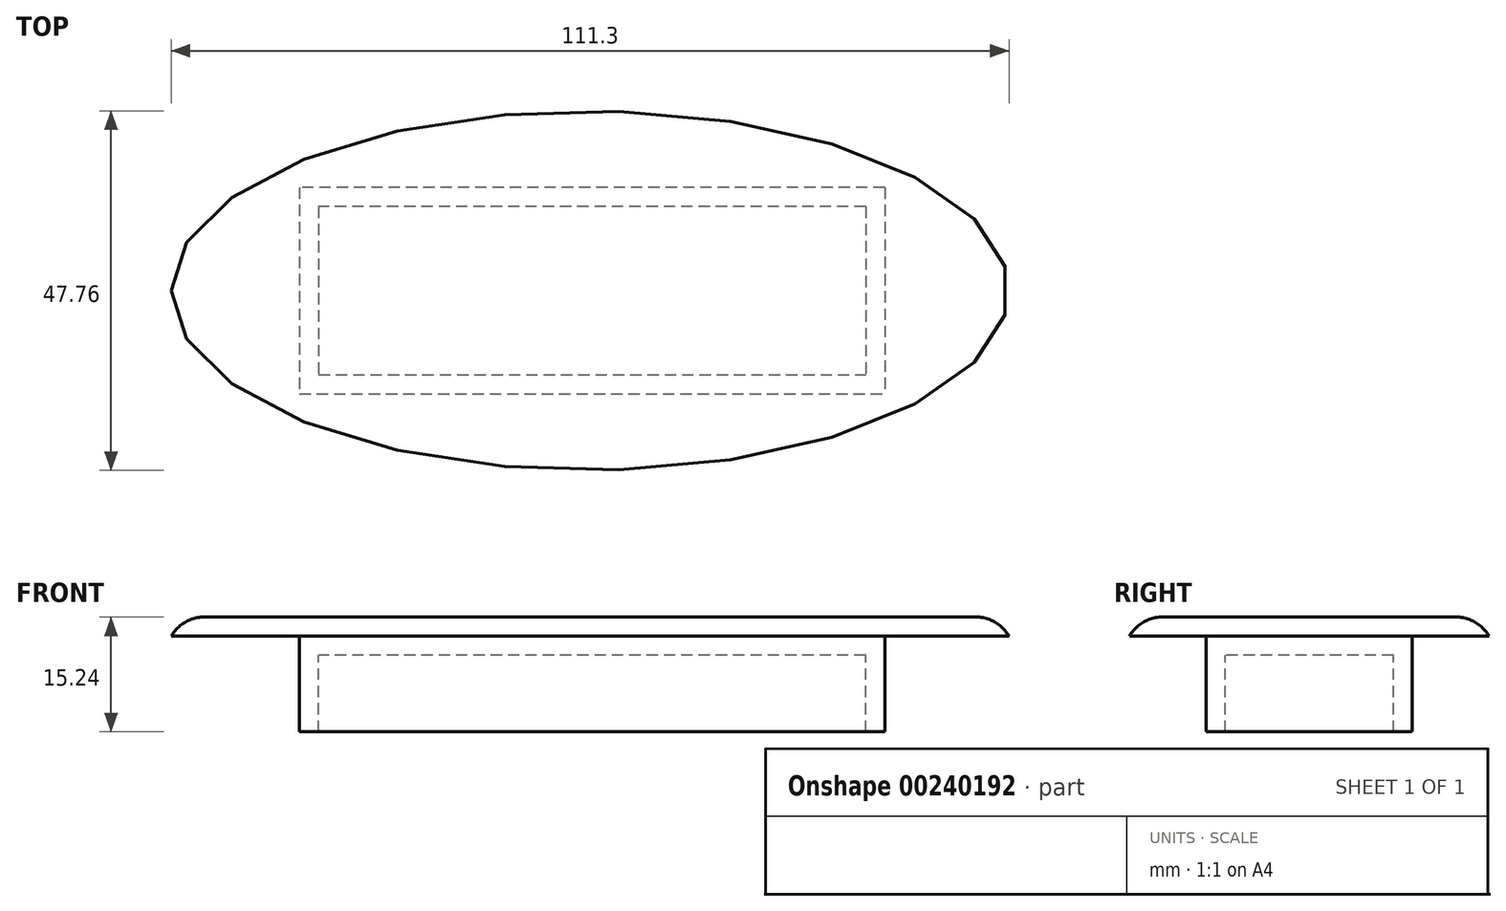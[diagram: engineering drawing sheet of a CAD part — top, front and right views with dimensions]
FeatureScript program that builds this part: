
annotation { "Feature Type Name" : "Feature", "Feature Type Description" : "" }
export const myFeature = defineFeature(function(context is Context, id is Id, definition is map)
    precondition{}
    {
        {
            var Q0;
            Q0=qCreatedBy(makeId("Top.planeOp"),FACE);
            var sketch = newSketch(context, id + "F0", { "sketchPlane" : qUnion([Q0])});
            skEllipse(sketch, "E0", {"center": v(0, 0) * mm, "majorRadius": 55.65 * mm, "minorRadius": 23.88 * mm, "majorAxis": v(-1, 0)});
            skSolve(sketch);
        }
        {
            var Q0;
            Q0 = qSketchRegion(id + "F0", true);
            extrude(context, id + "F1", {"entities" : qUnion([Q0]), "depth" : 2.54 * mm});
        }
        {
            var Q0;
            Q0=makeQuery(id+"F1.opExtrude","CAP_FACE",FACE,{"disambiguationData":[OSD([sQuery(id+"F0.wireOp",EDGE,"E0")])],"isStart":false});
            fillet(context, id + "F2", {"entities" : qUnion([Q0]), "radius" : 5.08 * mm, "tangentPropagation" : true, "allowEdgeOverflow" : false});
        }
        {
            var Q0;
            Q0=makeQuery(id+"F1.opExtrude","CAP_FACE",FACE,{"disambiguationData":[OSD([sQuery(id+"F0.wireOp",EDGE,"E0")])],"isStart":true});
            var sketch = newSketch(context, id + "F3", { "sketchPlane" : qUnion([Q0])});
            skLineSegment(sketch, "E1.bottom", {"start": v(-38.6, 0) * mm, "end": v(39.14, 0) * mm});
            skLineSegment(sketch, "E1.top", {"start": v(-38.6, 13.71) * mm, "end": v(39.14, 13.71) * mm});
            skLineSegment(sketch, "E1.left", {"start": v(-38.6, 0) * mm, "end": v(-38.6, 13.71) * mm});
            skLineSegment(sketch, "E1.right", {"start": v(39.14, 0) * mm, "end": v(39.14, 13.71) * mm});
            skLineSegment(sketch, "E2.bottom", {"start": v(39.14, 0) * mm, "end": v(-38.6, 0) * mm});
            skLineSegment(sketch, "E2.top", {"start": v(39.14, -13.71) * mm, "end": v(-38.6, -13.71) * mm});
            skLineSegment(sketch, "E2.left", {"start": v(39.14, 0) * mm, "end": v(39.14, -13.71) * mm});
            skLineSegment(sketch, "E2.right", {"start": v(-38.6, 0) * mm, "end": v(-38.6, -13.71) * mm});
            skSolve(sketch);
        }
        {
            var Q0;
            Q0 = qSketchRegion(id + "F3", true);
            extrude(context, id + "F4", {"entities" : qUnion([Q0]), "depth" : 12.7 * mm});
        }
        {
            var Q0;
            Q0=makeQuery(id+"F4.opExtrude","CAP_FACE",FACE,{"disambiguationData":[OSD([sQuery(id+"F3.wireOp",EDGE,"E1.top"),sQuery(id+"F3.wireOp",EDGE,"E1.left"),sQuery(id+"F3.wireOp",EDGE,"E1.right"),sQuery(id+"F3.wireOp",EDGE,"E2.top"),sQuery(id+"F3.wireOp",EDGE,"E2.left"),sQuery(id+"F3.wireOp",EDGE,"E2.right")])],"isStart":false});
            shell(context, id + "F5", {"entities" : qUnion([Q0]), "thickness" : 2.54 * mm});
        }
    });
